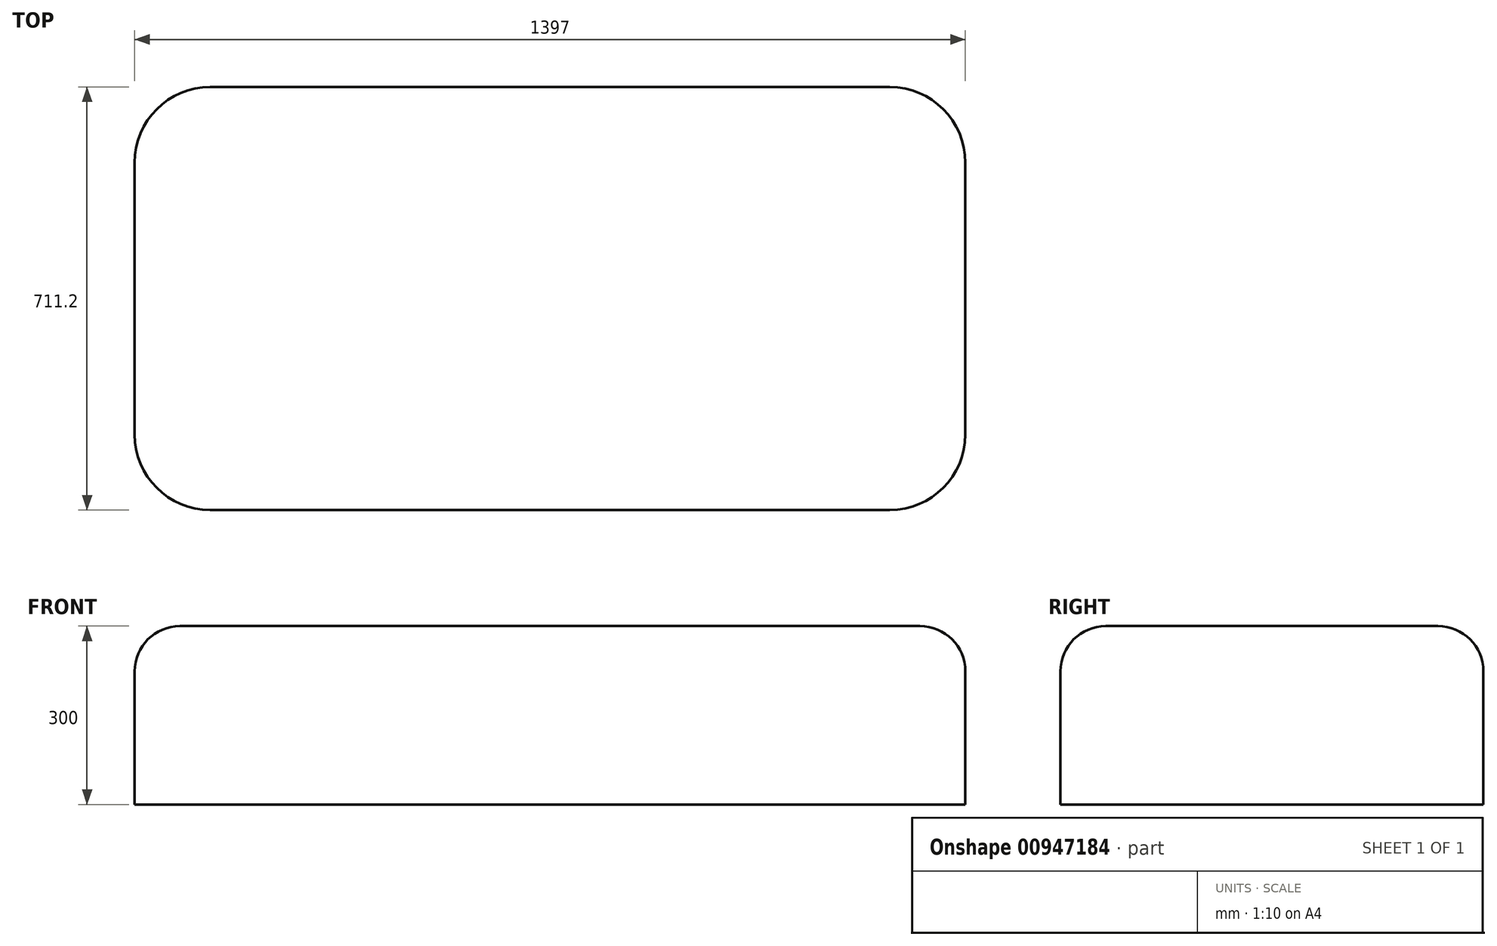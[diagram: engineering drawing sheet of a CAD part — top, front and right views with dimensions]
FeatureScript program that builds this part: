
annotation { "Feature Type Name" : "Feature", "Feature Type Description" : "" }
export const myFeature = defineFeature(function(context is Context, id is Id, definition is map)
    precondition{}
    {
        {
            var Q0;
            Q0=qCreatedBy(makeId("Top.planeOp"),FACE);
            var sketch = newSketch(context, id + "F0", { "sketchPlane" : qUnion([Q0])});
            skLineSegment(sketch, "E0.bottom", {"start": v(-127, 0) * mm, "end": v(-1270, 0) * mm});
            skLineSegment(sketch, "E0.top", {"start": v(-127, 711.2) * mm, "end": v(-1270, 711.2) * mm});
            skLineSegment(sketch, "E0.left", {"start": v(0, 127) * mm, "end": v(0, 584.2) * mm});
            skLineSegment(sketch, "E0.right", {"start": v(-1397, 127) * mm, "end": v(-1397, 584.2) * mm});
            skPoint(sketch, "E1.visualSharp", {"position": v(-1397, 711.2) * mm});
            skArc(sketch, "E1.filletArc", {"start": v(-1270, 711.2) * mm, "mid": v(-1359.8, 674) * mm, "end": v(-1397, 584.2) * mm});
            skPoint(sketch, "E2.visualSharp", {"position": v(0, 711.2) * mm});
            skArc(sketch, "E2.filletArc", {"start": v(0, 584.2) * mm, "mid": v(-37.2, 674) * mm, "end": v(-127, 711.2) * mm});
            skPoint(sketch, "E3.visualSharp", {"position": v(0, 0) * mm});
            skArc(sketch, "E3.filletArc", {"start": v(-127, 0) * mm, "mid": v(-37.2, 37.2) * mm, "end": v(0, 127) * mm});
            skPoint(sketch, "E4.visualSharp", {"position": v(-1397, 0) * mm});
            skArc(sketch, "E4.filletArc", {"start": v(-1397, 127) * mm, "mid": v(-1359.8, 37.2) * mm, "end": v(-1270, 0) * mm});
            skSolve(sketch);
        }
        {
            var Q0;
            Q0 = qSketchRegion(id + "F0", true);
            extrude(context, id + "F1", {"entities" : qUnion([Q0]), "depth" : 300 * mm, "offsetDistance" : 25.4 * mm});
        }
        {
            var Q0;
            Q0=makeQuery(id+"F1.opExtrude","CAP_FACE",FACE,{"disambiguationData":[OSD([sQuery(id+"F0.wireOp",EDGE,"E0.bottom"),sQuery(id+"F0.wireOp",EDGE,"E0.top"),sQuery(id+"F0.wireOp",EDGE,"E0.left"),sQuery(id+"F0.wireOp",EDGE,"E0.right"),sQuery(id+"F0.wireOp",EDGE,"E1.filletArc"),sQuery(id+"F0.wireOp",EDGE,"E2.filletArc"),sQuery(id+"F0.wireOp",EDGE,"E3.filletArc"),sQuery(id+"F0.wireOp",EDGE,"E4.filletArc")])],"isStart":false});
            fillet(context, id + "F2", {"entities" : qUnion([Q0]), "radius" : 76.2 * mm, "tangentPropagation" : true, "allowEdgeOverflow" : false});
        }
    });
